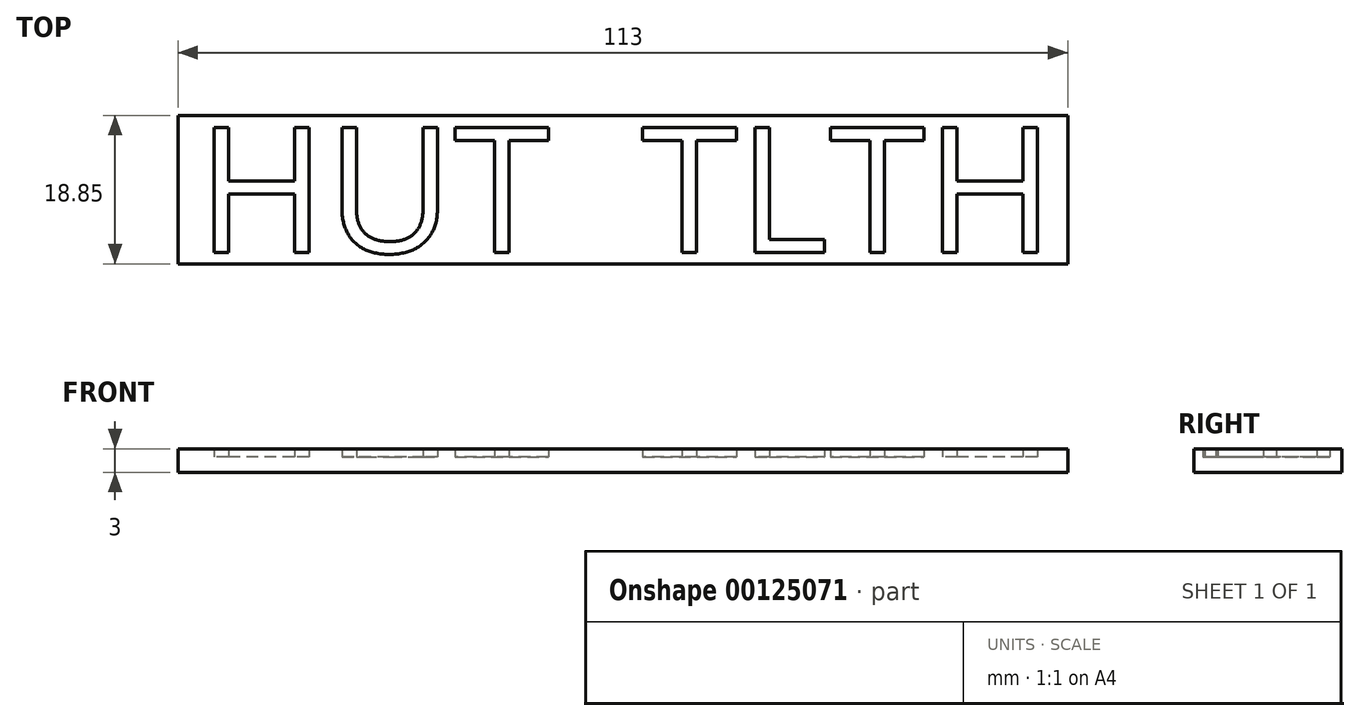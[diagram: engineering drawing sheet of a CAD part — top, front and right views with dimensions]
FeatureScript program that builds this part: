
annotation { "Feature Type Name" : "Feature", "Feature Type Description" : "" }
export const myFeature = defineFeature(function(context is Context, id is Id, definition is map)
    precondition{}
    {
        {
            var Q0;
            Q0=qCreatedBy(makeId("Top.planeOp"),FACE);
            var sketch = newSketch(context, id + "F0", { "sketchPlane" : qUnion([Q0])});
            skLineSegment(sketch, "E0.bottom", {"start": v(-79.58, 35.29) * mm, "end": v(33.42, 35.29) * mm});
            skLineSegment(sketch, "E0.top", {"start": v(-79.58, 16.44) * mm, "end": v(33.42, 16.44) * mm});
            skLineSegment(sketch, "E0.left", {"start": v(-79.58, 35.29) * mm, "end": v(-79.58, 16.44) * mm});
            skLineSegment(sketch, "E0.right", {"start": v(33.42, 35.29) * mm, "end": v(33.42, 16.44) * mm});
            skText(sketch, "E1", { "text": "HUT  TLTH", "fontName": "OpenSans-Regular.ttf"});
            const initialGuessF0  = {"E1": [-0.07719, 0.01786, 1, 0, 0.016]};
            skSetInitialGuess(sketch, initialGuessF0);
            skSolve(sketch);
        }
        {
            var Q0;
            Q0=makeQuery(id+"F0.imprint","IMPRINT",FACE,{"disambiguationData":[TD([[makeQuery(id+"F0.imprint","IMPRINT",EDGE,{"derivedFrom":sQuery(id+"F0.wireOp",EDGE,"E0.bottom")}),-1.0]])]});
            extrude(context, id + "F1", {"entities" : qUnion([Q0]), "depth" : 3 * mm});
        }
        {
            var Q0;
            Q0=makeQuery(id+"F0.imprint","IMPRINT",FACE,{"disambiguationData":[TD([[makeQuery(id+"F0.imprint","IMPRINT",EDGE,{"derivedFrom":sQuery(id+"F0.wireOp",EDGE,"E1.sketch_text.stroke-0")}),-1.0]])]});
            var Q1;
            Q1=makeQuery(id+"F0.imprint","IMPRINT",FACE,{"disambiguationData":[TD([[makeQuery(id+"F0.imprint","IMPRINT",EDGE,{"derivedFrom":sQuery(id+"F0.wireOp",EDGE,"E1.sketch_text.stroke-12")}),-1.0]])]});
            var Q2;
            Q2=makeQuery(id+"F0.imprint","IMPRINT",FACE,{"disambiguationData":[TD([[makeQuery(id+"F0.imprint","IMPRINT",EDGE,{"derivedFrom":sQuery(id+"F0.wireOp",EDGE,"E1.sketch_text.stroke-26")}),-1.0]])]});
            var Q3;
            Q3=makeQuery(id+"F0.imprint","IMPRINT",FACE,{"disambiguationData":[TD([[makeQuery(id+"F0.imprint","IMPRINT",EDGE,{"derivedFrom":sQuery(id+"F0.wireOp",EDGE,"E1.sketch_text.stroke-34")}),-1.0]])]});
            var Q4;
            Q4=makeQuery(id+"F0.imprint","IMPRINT",FACE,{"disambiguationData":[TD([[makeQuery(id+"F0.imprint","IMPRINT",EDGE,{"derivedFrom":sQuery(id+"F0.wireOp",EDGE,"E1.sketch_text.stroke-42")}),-1.0]])]});
            var Q5;
            Q5=makeQuery(id+"F0.imprint","IMPRINT",FACE,{"disambiguationData":[TD([[makeQuery(id+"F0.imprint","IMPRINT",EDGE,{"derivedFrom":sQuery(id+"F0.wireOp",EDGE,"E1.sketch_text.stroke-48")}),-1.0]])]});
            var Q6;
            Q6=makeQuery(id+"F0.imprint","IMPRINT",FACE,{"disambiguationData":[TD([[makeQuery(id+"F0.imprint","IMPRINT",EDGE,{"derivedFrom":sQuery(id+"F0.wireOp",EDGE,"E1.sketch_text.stroke-56")}),-1.0]])]});
            extrude(context, id + "F2", {"entities" : qUnion([Q0, Q1, Q2, Q3, Q4, Q5, Q6]), "operationType" : NewBodyOperationType.ADD, "depth" : 2 * mm});
        }
    });
